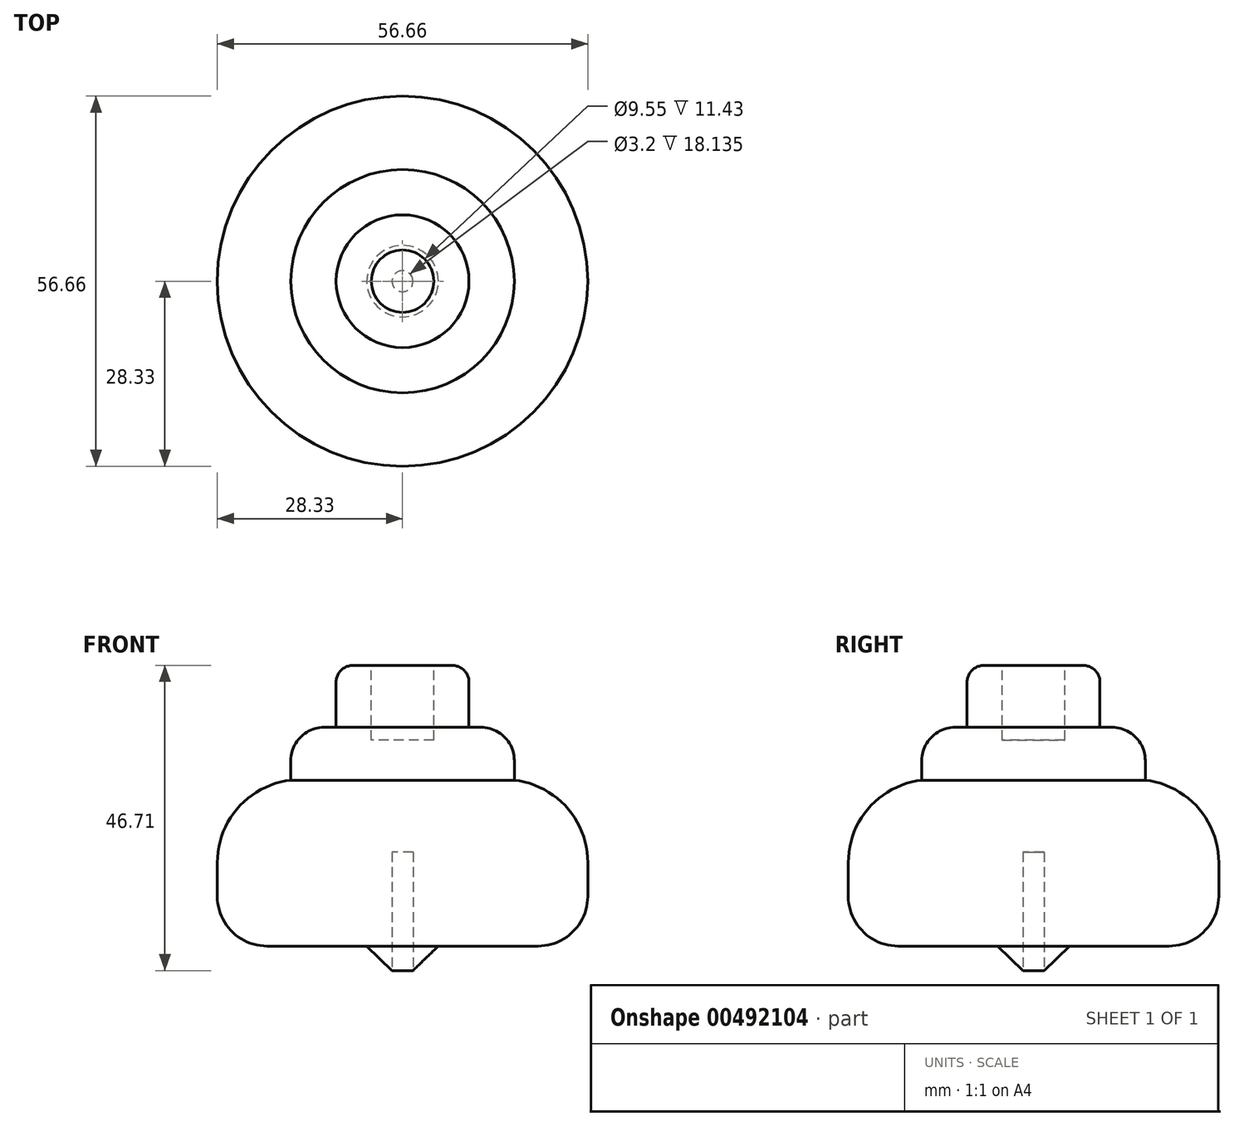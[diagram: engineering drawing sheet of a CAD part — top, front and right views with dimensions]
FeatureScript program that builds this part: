
annotation { "Feature Type Name" : "Feature", "Feature Type Description" : "" }
export const myFeature = defineFeature(function(context is Context, id is Id, definition is map)
    precondition{}
    {
        {
            var Q0;
            Q0=qCreatedBy(makeId("Front.planeOp"),FACE);
            var sketch = newSketch(context, id + "F0", { "sketchPlane" : qUnion([Q0])});
            skLineSegment(sketch, "E0", {"start": v(0, 0) * mm, "end": v(5.47, 5.3) * mm});
            skLineSegment(sketch, "E1", {"start": v(5.47, 5.3) * mm, "end": v(28.33, 5.3) * mm});
            skLineSegment(sketch, "E2", {"start": v(28.33, 5.3) * mm, "end": v(28.33, 30.7) * mm});
            skLineSegment(sketch, "E3", {"start": v(28.33, 30.7) * mm, "end": v(17.09, 30.7) * mm});
            skLineSegment(sketch, "E4", {"start": v(17.09, 30.7) * mm, "end": v(17.09, 38.8) * mm});
            skLineSegment(sketch, "E5", {"start": v(17.09, 38.8) * mm, "end": v(10.16, 38.8) * mm});
            skLineSegment(sketch, "E6", {"start": v(10.16, 38.8) * mm, "end": v(10.16, 48.26) * mm});
            skLineSegment(sketch, "E7", {"start": v(10.16, 48.26) * mm, "end": v(0, 48.26) * mm});
            skLineSegment(sketch, "E8", {"start": v(0, 48.26) * mm, "end": v(0, 0) * mm});
            skSolve(sketch);
        }
        {
            var Q0;
            Q0=makeQuery(id+"F0.imprint","IMPRINT",FACE,{"disambiguationData":[TD([[makeQuery(id+"F0.imprint","IMPRINT",EDGE,{"derivedFrom":sQuery(id+"F0.wireOp",EDGE,"E0")}),1.0]])]});
            var Q1;
            Q1=sQuery(id+"F0.wireOp",EDGE,"E8");
            revolve(context, id + "F1", {"entities" : qUnion([Q0]), "axis" : qUnion([Q1]), "revolveType" : RevolveType.FULL});
        }
        {
            var Q0;
            Q0=makeQuery(id+"F1.opRevolve","SWEPT_EDGE",EDGE,{"disambiguationData":[OSD([sQuery(id+"F0.wireOp",EDGE,"E4"),sQuery(id+"F0.wireOp",EDGE,"E5")])]});
            fillet(context, id + "F2", {"entities" : qUnion([Q0]), "radius" : 5.08 * mm, "tangentPropagation" : true, "allowEdgeOverflow" : false});
        }
        {
            var Q0;
            Q0=makeQuery(id+"F1.opRevolve","SWEPT_EDGE",EDGE,{"disambiguationData":[OSD([sQuery(id+"F0.wireOp",EDGE,"E2"),sQuery(id+"F0.wireOp",EDGE,"E3")])]});
            fillet(context, id + "F3", {"entities" : qUnion([Q0]), "radius" : 12.7 * mm, "tangentPropagation" : true, "allowEdgeOverflow" : false});
        }
        {
            var Q0;
            Q0=makeQuery(id+"F1.opRevolve","SWEPT_EDGE",EDGE,{"disambiguationData":[OSD([sQuery(id+"F0.wireOp",EDGE,"E1"),sQuery(id+"F0.wireOp",EDGE,"E2")])]});
            fillet(context, id + "F4", {"entities" : qUnion([Q0]), "radius" : 7.62 * mm, "tangentPropagation" : true, "allowEdgeOverflow" : false});
        }
        {
            var Q0;
            Q0=makeQuery(id+"F1.opRevolve","SWEPT_EDGE",EDGE,{"disambiguationData":[OSD([sQuery(id+"F0.wireOp",EDGE,"E6"),sQuery(id+"F0.wireOp",EDGE,"E7")])]});
            fillet(context, id + "F5", {"entities" : qUnion([Q0]), "radius" : 2.54 * mm, "tangentPropagation" : true, "allowEdgeOverflow" : false});
        }
        {
            var Q0;
            Q0=makeQuery(id+"F1.opRevolve","SWEPT_FACE",FACE,{"disambiguationData":[OSD([sQuery(id+"F0.wireOp",EDGE,"E7")])]});
            var sketch = newSketch(context, id + "F6", { "sketchPlane" : qUnion([Q0])});
            skCircle(sketch, "E9", {"center": v(0, 0) * mm, "radius": 4.78 * mm});
            skSolve(sketch);
        }
        {
            var Q0;
            Q0=makeQuery(id+"F6.imprint","IMPRINT",FACE,{"disambiguationData":[TD([[makeQuery(id+"F6.imprint","IMPRINT",EDGE,{"derivedFrom":sQuery(id+"F6.wireOp",EDGE,"E9")}),1.0]])]});
            var Q1;
            Q1=sQuery(id+"F6.wireOp",EDGE,"E9");
            extrude(context, id + "F7", {"entities" : qUnion([Q0]), "operationType" : NewBodyOperationType.REMOVE, "surfaceEntities" : qUnion([Q1]), "oppositeDirection" : true, "depth" : 11.43 * mm});
        }
        {
            var Q0;
            Q0=qCreatedBy(makeId("Top.planeOp"),FACE);
            var sketch = newSketch(context, id + "F8", { "sketchPlane" : qUnion([Q0])});
            skCircle(sketch, "E10", {"center": v(0, 0) * mm, "radius": 1.6 * mm});
            skSolve(sketch);
        }
        {
            var Q0;
            Q0=makeQuery(id+"F8.imprint","IMPRINT",FACE,{"disambiguationData":[TD([[makeQuery(id+"F8.imprint","IMPRINT",EDGE,{"derivedFrom":sQuery(id+"F8.wireOp",EDGE,"E10")}),1.0]])]});
            extrude(context, id + "F9", {"entities" : qUnion([Q0]), "operationType" : NewBodyOperationType.REMOVE, "depth" : 19.68 * mm});
        }
    });
